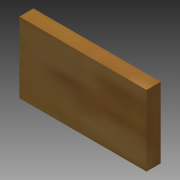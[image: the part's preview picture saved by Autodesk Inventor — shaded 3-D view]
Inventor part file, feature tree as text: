
AUTODESK INVENTOR PART (.ipt)
format: ipt  version: 2013 (Build 170138000, 138)  size: 80,896 bytes
history: native  units: in
note: dims shown in document units (in); Inventor stores cm internally (conversion verified against a paired STEP export)
features: extrude x1, sketch x1
ambient origin geometry x8: Origin, YZ Plane, XZ Plane, XY Plane, X Axis, Y Axis, Z Axis, Center Point
bodies: Solid1 (feature_tree)
feature tree (2):
  extrude  "Extrusion1"  Depth=1.25in
  sketch  "Sketch1"  dims[d0=2.25in d2=1.25in d3=0.25in d4=0.0in]
